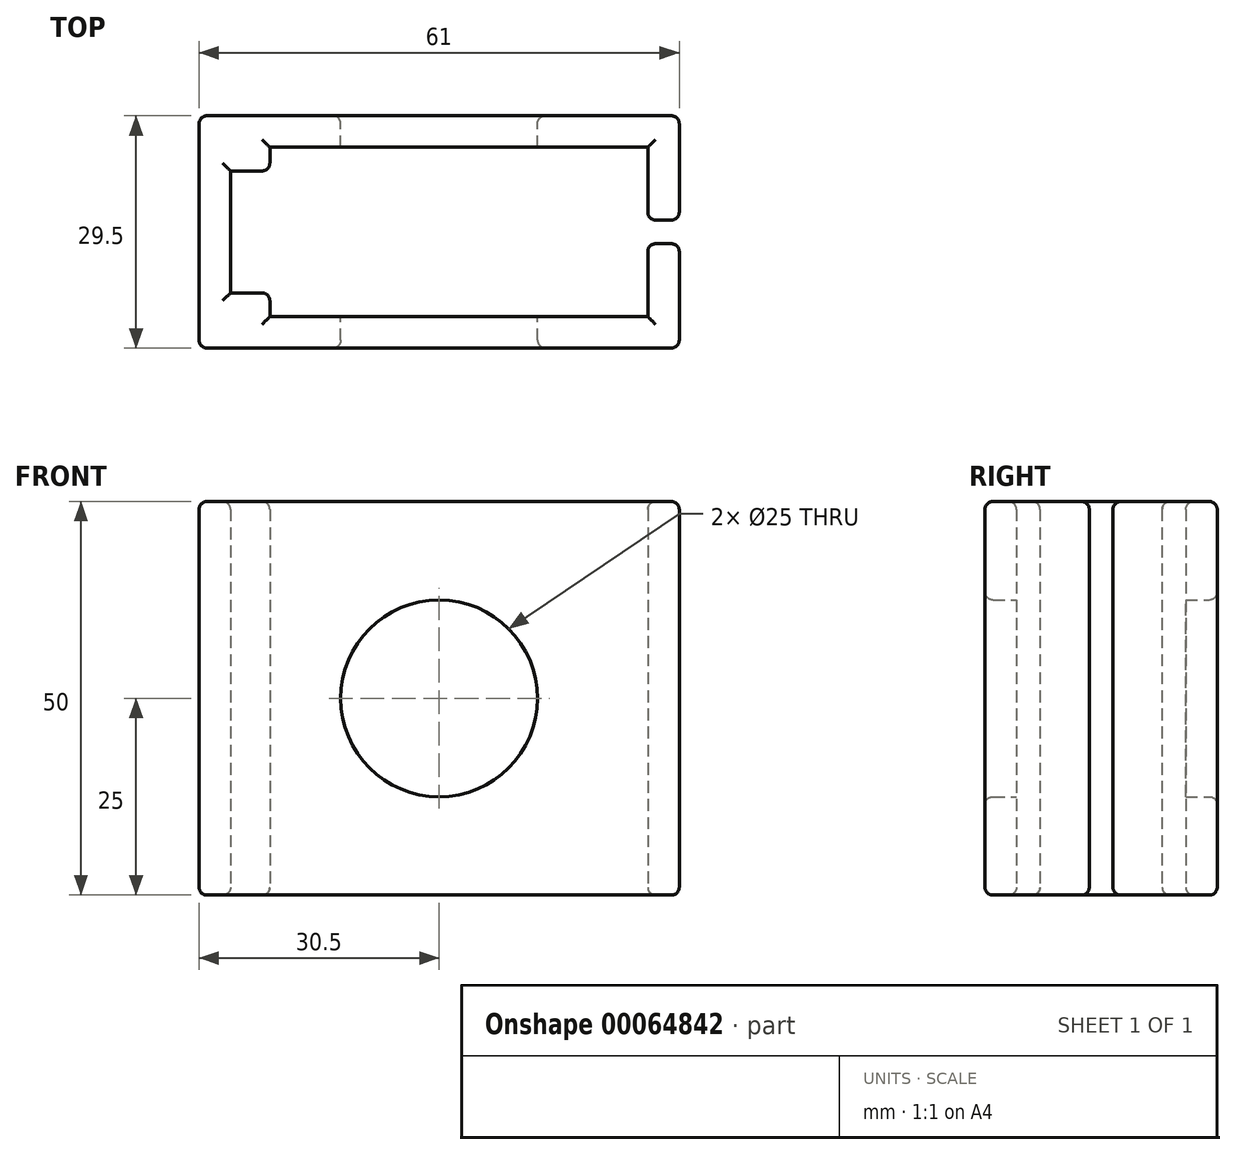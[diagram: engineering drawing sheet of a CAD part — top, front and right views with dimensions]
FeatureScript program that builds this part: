
annotation { "Feature Type Name" : "Feature", "Feature Type Description" : "" }
export const myFeature = defineFeature(function(context is Context, id is Id, definition is map)
    precondition{}
    {
        {
            var Q0;
            Q0=qCreatedBy(makeId("Top.planeOp"),FACE);
            var sketch = newSketch(context, id + "F0", { "sketchPlane" : qUnion([Q0])});
            skLineSegment(sketch, "E0", {"start": v(61, 0) * mm, "end": v(0, 0) * mm});
            skLineSegment(sketch, "E1", {"start": v(0, 0) * mm, "end": v(0, 29.5) * mm});
            skLineSegment(sketch, "E2", {"start": v(0, 29.5) * mm, "end": v(61, 29.5) * mm});
            skLineSegment(sketch, "E3", {"start": v(61, 29.5) * mm, "end": v(61, 16.25) * mm});
            skLineSegment(sketch, "E4", {"start": v(61, 16.25) * mm, "end": v(57, 16.25) * mm});
            skLineSegment(sketch, "E5", {"start": v(57, 16.25) * mm, "end": v(57, 25.5) * mm});
            skLineSegment(sketch, "E6", {"start": v(57, 25.5) * mm, "end": v(9, 25.5) * mm});
            skLineSegment(sketch, "E7", {"start": v(9, 4) * mm, "end": v(57, 4) * mm});
            skLineSegment(sketch, "E8", {"start": v(57, 4) * mm, "end": v(57, 13.25) * mm});
            skLineSegment(sketch, "E9", {"start": v(57, 13.25) * mm, "end": v(61, 13.25) * mm});
            skLineSegment(sketch, "E10", {"start": v(61, 13.25) * mm, "end": v(61, 0) * mm});
            skLineSegment(sketch, "E11", {"start": v(9, 25.5) * mm, "end": v(9, 22.5) * mm});
            skLineSegment(sketch, "E12", {"start": v(9, 22.5) * mm, "end": v(4, 22.5) * mm});
            skLineSegment(sketch, "E13", {"start": v(4, 22.5) * mm, "end": v(4, 7) * mm});
            skLineSegment(sketch, "E14", {"start": v(4, 7) * mm, "end": v(9, 7) * mm});
            skLineSegment(sketch, "E15", {"start": v(9, 7) * mm, "end": v(9, 4) * mm});
            skSolve(sketch);
        }
        {
            var Q0;
            Q0 = qSketchRegion(id + "F0", true);
            extrude(context, id + "F1", {"entities" : qUnion([Q0]), "depth" : 50 * mm});
        }
        {
            var Q0;
            Q0=makeQuery(id+"F1.opExtrude","SWEPT_FACE",FACE,{"disambiguationData":[OSD([sQuery(id+"F0.wireOp",EDGE,"E2")])]});
            var sketch = newSketch(context, id + "F2", { "sketchPlane" : qUnion([Q0])});
            skCircle(sketch, "E16", {"center": v(-30.5, 25) * mm, "radius": 12.5 * mm});
            skLineSegment(sketch, "E17", {"start": v(-30.5, 25) * mm, "end": v(-1, 25) * mm, "construction": true});
            skLineSegment(sketch, "E18", {"start": v(-30.5, 1) * mm, "end": v(-30.5, 25) * mm, "construction": true});
            skSolve(sketch);
        }
        {
            var Q0;
            Q0 = qSketchRegion(id + "F2", true);
            extrude(context, id + "F3", {"entities" : qUnion([Q0]), "operationType" : NewBodyOperationType.REMOVE, "endBound" : BoundingType.THROUGH_ALL, "oppositeDirection" : true, "depth" : 25 * mm});
        }
        {
            var Q0;
            Q0=makeQuery(id+"F1.opExtrude","CAP_EDGE",EDGE,{"disambiguationData":[OSD([sQuery(id+"F0.wireOp",EDGE,"E5")])],"isStart":true});
            var Q1;
            Q1=makeQuery(id+"F1.opExtrude","CAP_EDGE",EDGE,{"disambiguationData":[OSD([sQuery(id+"F0.wireOp",EDGE,"E6")])],"isStart":true});
            var Q2;
            Q2=makeQuery(id+"F1.opExtrude","CAP_EDGE",EDGE,{"disambiguationData":[OSD([sQuery(id+"F0.wireOp",EDGE,"E11")])],"isStart":true});
            var Q3;
            Q3=makeQuery(id+"F1.opExtrude","CAP_EDGE",EDGE,{"disambiguationData":[OSD([sQuery(id+"F0.wireOp",EDGE,"E12")])],"isStart":true});
            var Q4;
            Q4=makeQuery(id+"F1.opExtrude","CAP_EDGE",EDGE,{"disambiguationData":[OSD([sQuery(id+"F0.wireOp",EDGE,"E13")])],"isStart":true});
            var Q5;
            Q5=makeQuery(id+"F1.opExtrude","CAP_EDGE",EDGE,{"disambiguationData":[OSD([sQuery(id+"F0.wireOp",EDGE,"E14")])],"isStart":true});
            var Q6;
            Q6=makeQuery(id+"F1.opExtrude","CAP_EDGE",EDGE,{"disambiguationData":[OSD([sQuery(id+"F0.wireOp",EDGE,"E15")])],"isStart":true});
            var Q7;
            Q7=makeQuery(id+"F1.opExtrude","CAP_EDGE",EDGE,{"disambiguationData":[OSD([sQuery(id+"F0.wireOp",EDGE,"E7")])],"isStart":true});
            var Q8;
            Q8=makeQuery(id+"F1.opExtrude","CAP_EDGE",EDGE,{"disambiguationData":[OSD([sQuery(id+"F0.wireOp",EDGE,"E8")])],"isStart":true});
            fillet(context, id + "F4", {"entities" : qUnion([Q0, Q1, Q2, Q3, Q4, Q5, Q6, Q7, Q8]), "radius" : 1 * mm, "tangentPropagation" : true, "allowEdgeOverflow" : false});
        }
        {
            var Q0;
            Q0=makeQuery(id+"F1.opExtrude","CAP_EDGE",EDGE,{"disambiguationData":[OSD([sQuery(id+"F0.wireOp",EDGE,"E6")])],"isStart":false});
            var Q1;
            Q1=makeQuery(id+"F1.opExtrude","CAP_EDGE",EDGE,{"disambiguationData":[OSD([sQuery(id+"F0.wireOp",EDGE,"E11")])],"isStart":false});
            var Q2;
            Q2=makeQuery(id+"F1.opExtrude","CAP_EDGE",EDGE,{"disambiguationData":[OSD([sQuery(id+"F0.wireOp",EDGE,"E13")])],"isStart":false});
            var Q3;
            Q3=makeQuery(id+"F1.opExtrude","CAP_EDGE",EDGE,{"disambiguationData":[OSD([sQuery(id+"F0.wireOp",EDGE,"E14")])],"isStart":false});
            var Q4;
            Q4=makeQuery(id+"F1.opExtrude","CAP_EDGE",EDGE,{"disambiguationData":[OSD([sQuery(id+"F0.wireOp",EDGE,"E15")])],"isStart":false});
            var Q5;
            Q5=makeQuery(id+"F1.opExtrude","CAP_EDGE",EDGE,{"disambiguationData":[OSD([sQuery(id+"F0.wireOp",EDGE,"E7")])],"isStart":false});
            var Q6;
            Q6=makeQuery(id+"F1.opExtrude","CAP_EDGE",EDGE,{"disambiguationData":[OSD([sQuery(id+"F0.wireOp",EDGE,"E5")])],"isStart":false});
            var Q7;
            Q7=makeQuery(id+"F1.opExtrude","CAP_EDGE",EDGE,{"disambiguationData":[OSD([sQuery(id+"F0.wireOp",EDGE,"E8")])],"isStart":false});
            fillet(context, id + "F5", {"entities" : qUnion([Q0, Q1, Q2, Q3, Q4, Q5, Q6, Q7]), "radius" : 1 * mm, "tangentPropagation" : true, "allowEdgeOverflow" : false});
        }
        {
            var Q0;
            Q0=makeQuery(id+"F1.opExtrude","SWEPT_FACE",FACE,{"disambiguationData":[OSD([sQuery(id+"F0.wireOp",EDGE,"E2")])]});
            var Q1;
            Q1=makeQuery(id+"F1.opExtrude","SWEPT_FACE",FACE,{"disambiguationData":[OSD([sQuery(id+"F0.wireOp",EDGE,"E1")])]});
            var Q2;
            Q2=makeQuery(id+"F1.opExtrude","SWEPT_FACE",FACE,{"disambiguationData":[OSD([sQuery(id+"F0.wireOp",EDGE,"E0")])]});
            var Q3;
            Q3=makeQuery(id+"F1.opExtrude","SWEPT_FACE",FACE,{"disambiguationData":[OSD([sQuery(id+"F0.wireOp",EDGE,"E10")])]});
            var Q4;
            Q4=makeQuery(id+"F1.opExtrude","SWEPT_FACE",FACE,{"disambiguationData":[OSD([sQuery(id+"F0.wireOp",EDGE,"E3")])]});
            var Q5;
            Q5=makeQuery(id+"F1.opExtrude","SWEPT_EDGE",EDGE,{"disambiguationData":[OSD([sQuery(id+"F0.wireOp",EDGE,"E14"),sQuery(id+"F0.wireOp",EDGE,"E15")])]});
            var Q6;
            Q6=makeQuery(id+"F1.opExtrude","SWEPT_EDGE",EDGE,{"disambiguationData":[OSD([sQuery(id+"F0.wireOp",EDGE,"E11"),sQuery(id+"F0.wireOp",EDGE,"E12")])]});
            var Q7;
            Q7=makeQuery(id+"F1.opExtrude","SWEPT_EDGE",EDGE,{"disambiguationData":[OSD([sQuery(id+"F0.wireOp",EDGE,"E4"),sQuery(id+"F0.wireOp",EDGE,"E5")])]});
            var Q8;
            Q8=makeQuery(id+"F1.opExtrude","SWEPT_EDGE",EDGE,{"disambiguationData":[OSD([sQuery(id+"F0.wireOp",EDGE,"E8"),sQuery(id+"F0.wireOp",EDGE,"E9")])]});
            fillet(context, id + "F6", {"entities" : qUnion([Q0, Q1, Q2, Q3, Q4, Q5, Q6, Q7, Q8]), "radius" : 1 * mm, "tangentPropagation" : true, "allowEdgeOverflow" : false});
        }
    });
